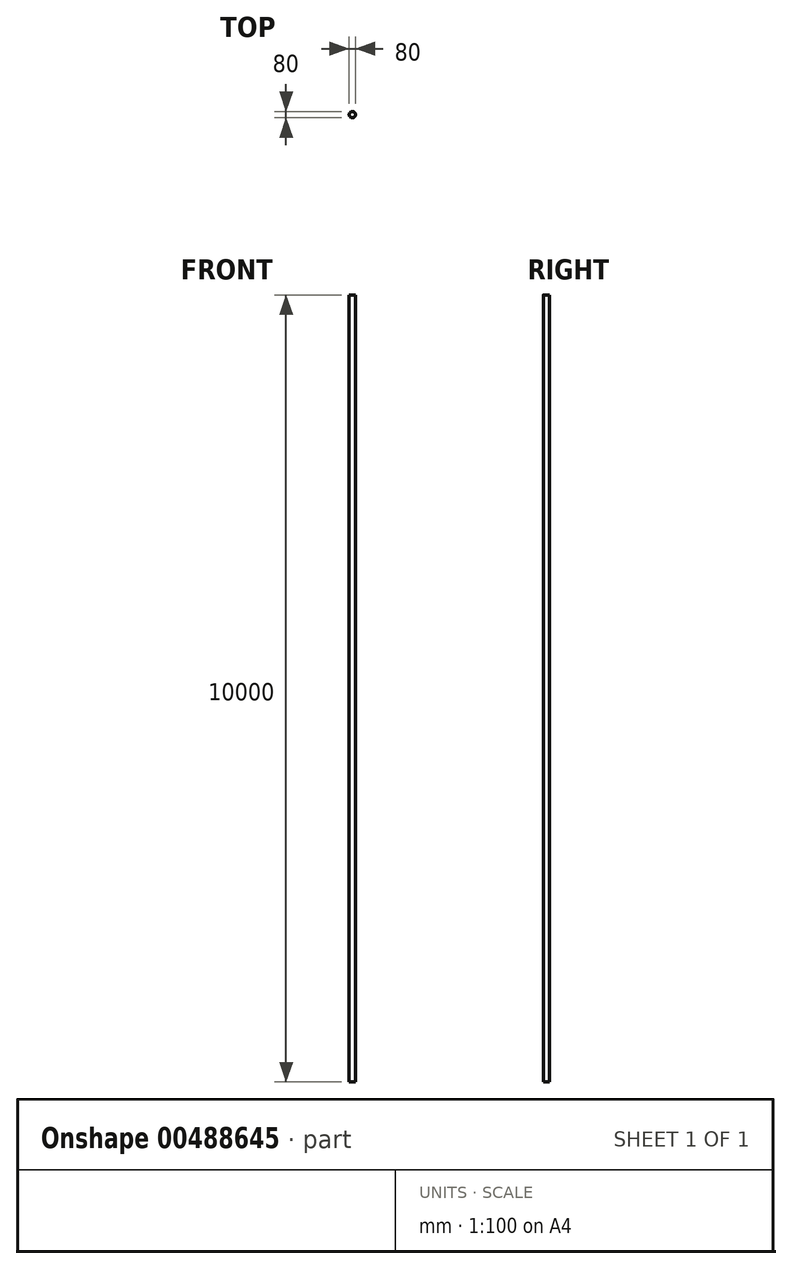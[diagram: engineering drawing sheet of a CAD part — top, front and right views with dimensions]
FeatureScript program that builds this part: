
annotation { "Feature Type Name" : "Feature", "Feature Type Description" : "" }
export const myFeature = defineFeature(function(context is Context, id is Id, definition is map)
    precondition{}
    {
        {
            var Q0;
            Q0=qCreatedBy(makeId("Top.planeOp"),FACE);
            var sketch = newSketch(context, id + "F0", { "sketchPlane" : qUnion([Q0])});
            skCircle(sketch, "E0", {"center": v(0, 0) * mm, "radius": 40 * mm});
            skSolve(sketch);
        }
        {
            var Q0;
            Q0 = qSketchRegion(id + "F0", true);
            extrude(context, id + "F1", {"entities" : qUnion([Q0]), "depth" : 10000 * mm});
        }
    });
